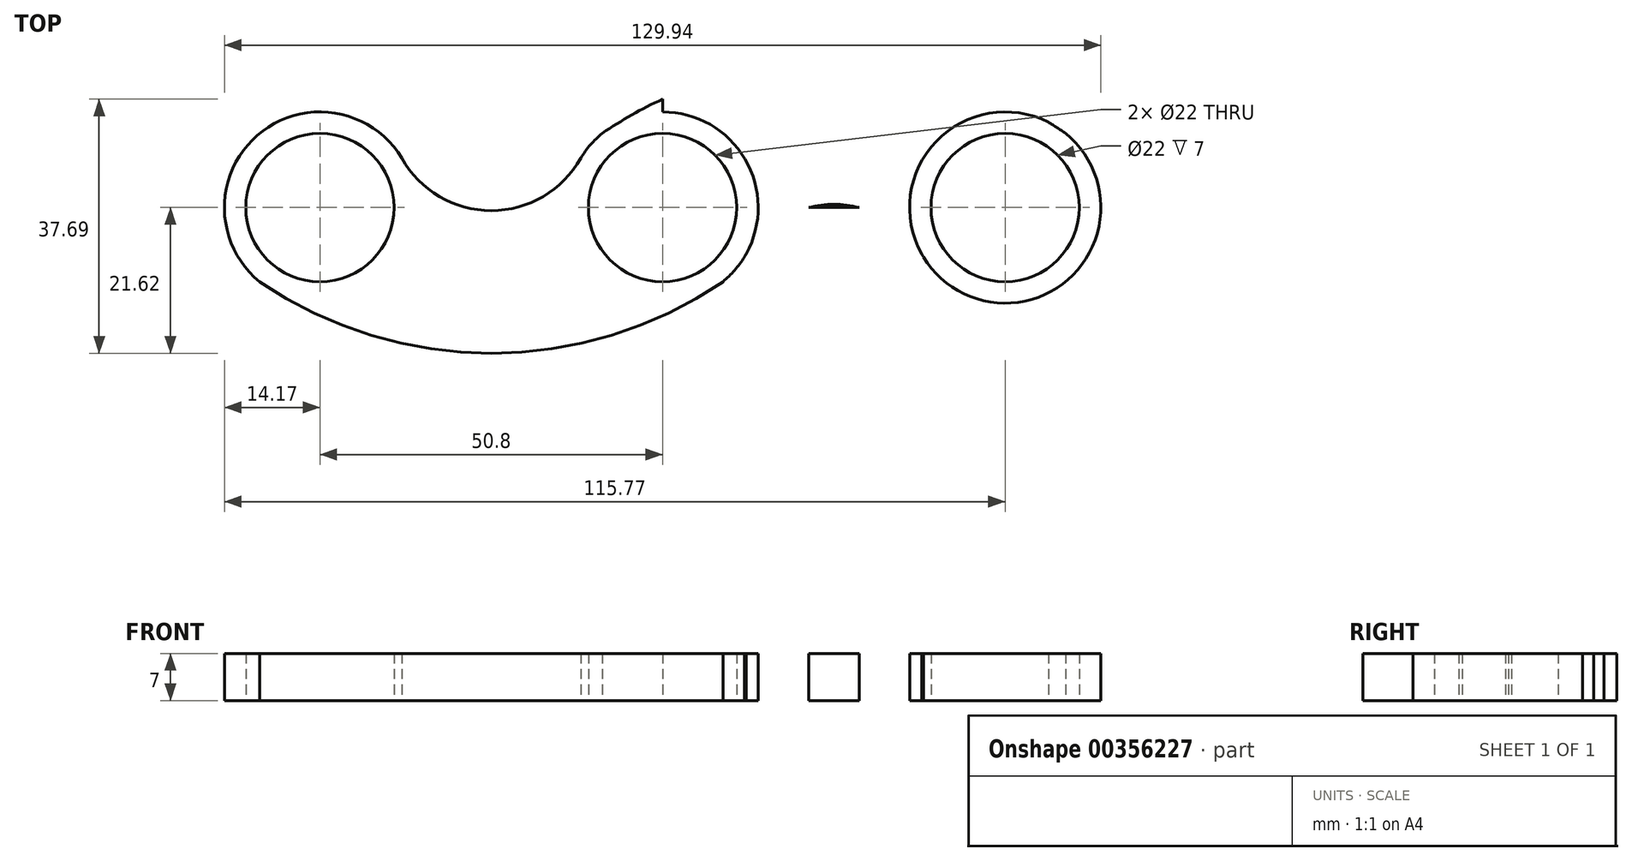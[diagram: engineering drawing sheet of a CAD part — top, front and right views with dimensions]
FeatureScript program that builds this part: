
annotation { "Feature Type Name" : "Feature", "Feature Type Description" : "" }
export const myFeature = defineFeature(function(context is Context, id is Id, definition is map)
    precondition{}
    {
        {
            var Q0;
            Q0=qCreatedBy(makeId("Top.planeOp"),FACE);
            var sketch = newSketch(context, id + "F0", { "sketchPlane" : qUnion([Q0])});
            skCircle(sketch, "E0", {"center": v(0, 0) * mm, "radius": 11 * mm});
            skLineSegment(sketch, "E1", {"start": v(0, 0) * mm, "end": v(-50.8, 0) * mm});
            skLineSegment(sketch, "E2", {"start": v(0, 0) * mm, "end": v(50.8, 0) * mm});
            skCircle(sketch, "E3", {"center": v(-50.8, 0) * mm, "radius": 11 * mm});
            skCircle(sketch, "E4", {"center": v(50.8, 0) * mm, "radius": 11 * mm});
            skCircle(sketch, "E5", {"center": v(-50.8, 0) * mm, "radius": 14.17 * mm});
            skCircle(sketch, "E6", {"center": v(50.8, 0) * mm, "radius": 14.17 * mm});
            skCircle(sketch, "E7", {"center": v(0, 0) * mm, "radius": 14.17 * mm});
            skPoint(sketch, "E8", {"position": v(0, 14.17) * mm});
            skPoint(sketch, "E9", {"position": v(-50.8, 14.17) * mm});
            skPoint(sketch, "E10", {"position": v(-41.86, 11) * mm});
            skPoint(sketch, "E11", {"position": v(-8.94, 11) * mm});
            skPoint(sketch, "E12", {"position": v(-38.67, 7.33) * mm});
            skPoint(sketch, "E13", {"position": v(-12.13, 7.33) * mm});
            skPoint(sketch, "E14", {"position": v(-29.14, 0) * mm});
            skArc(sketch, "E15", {"start": v(-38.67, 7.33) * mm, "mid": v(-25.4, -0.47) * mm, "end": v(-12.13, 7.33) * mm});
            skPoint(sketch, "E16", {"position": v(-59.74, -11) * mm});
            skPoint(sketch, "E17", {"position": v(8.94, -11) * mm});
            skPoint(sketch, "E18", {"position": v(-29.14, -21.5) * mm});
            skArc(sketch, "E19", {"start": v(-59.74, -11) * mm, "mid": v(-25.4, -21.62) * mm, "end": v(8.94, -11) * mm});
            skLineSegment(sketch, "E20", {"start": v(0, 55.32) * mm, "end": v(0, -62.03) * mm});
            skPoint(sketch, "E21", {"position": v(29.13, 0) * mm});
            skPoint(sketch, "E22", {"position": v(38.67, -7.34) * mm});
            skPoint(sketch, "E23", {"position": v(12.13, -7.34) * mm});
            skPoint(sketch, "E24", {"position": v(59.74, 11) * mm});
            skPoint(sketch, "E25", {"position": v(29.13, 21.51) * mm});
            skArc(sketch, "E26", {"start": v(59.74, 11) * mm, "mid": v(25.4, 21.63) * mm, "end": v(-8.94, 11) * mm});
            skArc(sketch, "E27", {"start": v(38.67, -7.34) * mm, "mid": v(25.4, 0.47) * mm, "end": v(12.13, -7.34) * mm});
            skSolve(sketch);
        }
        {
            var Q0;
            Q0=makeQuery(id+"F0.imprint","IMPRINT",FACE,{"disambiguationData":[TD([[makeQuery(id+"F0.imprint","IMPRINT",EDGE,{"derivedFrom":sQuery(id+"F0.wireOp",EDGE,"E4")}),-1.0]])]});
            var Q1;
            {var subQ1=sQuery(id+"F0.wireOp",EDGE,"E2");var subQ5=sQuery(id+"F0.wireOp",EDGE,"E27");var subQ6=makeQuery(id+"F0.imprint","INTERSECT",VERTEX,{"disambiguationData":[OD(0.0)],"derivedFrom":[subQ1,subQ5]});Q1=makeQuery(id+"F0.imprint","IMPRINT",FACE,{"disambiguationData":[TD([[makeQuery(id+"F0.imprint","IMPRINT",EDGE,{"disambiguationData":[TD([[subQ6,1.0]])],"derivedFrom":subQ1}),1.0]])]});}
            var Q2;
            {var subQ1=sQuery(id+"F0.wireOp",EDGE,"E1");var subQ9=sQuery(id+"F0.wireOp",EDGE,"E15");var subQ12=makeQuery(id+"F0.imprint","INTERSECT",VERTEX,{"disambiguationData":[OD(0.0)],"derivedFrom":[subQ1,subQ9]});Q2=makeQuery(id+"F0.imprint","IMPRINT",FACE,{"disambiguationData":[TD([[makeQuery(id+"F0.imprint","IMPRINT",EDGE,{"disambiguationData":[TD([[subQ12,1.0]])],"derivedFrom":subQ1}),1.0]])]});}
            var Q3;
            Q3=makeQuery(id+"F0.imprint","IMPRINT",FACE,{"disambiguationData":[TD([[makeQuery(id+"F0.imprint","IMPRINT",EDGE,{"derivedFrom":sQuery(id+"F0.wireOp",EDGE,"E3")}),-1.0]])]});
            var Q4;
            {var subQ6=sQuery(id+"F0.wireOp",EDGE,"E2");var subQ7=sQuery(id+"F0.wireOp",EDGE,"E0");var subQ8=makeQuery(id+"F0.imprint","INTERSECT",VERTEX,{"derivedFrom":[subQ7,subQ6]});Q4=makeQuery(id+"F0.imprint","IMPRINT",FACE,{"disambiguationData":[TD([[makeQuery(id+"F0.imprint","IMPRINT",EDGE,{"disambiguationData":[TD([[subQ8,1.0]])],"derivedFrom":subQ7}),-1.0]])]});}
            var Q5;
            {var subQ0=sQuery(id+"F0.wireOp",EDGE,"E1");var subQ1=sQuery(id+"F0.wireOp",EDGE,"E0");var subQ2=makeQuery(id+"F0.imprint","INTERSECT",VERTEX,{"derivedFrom":[subQ1,subQ0]});Q5=makeQuery(id+"F0.imprint","IMPRINT",FACE,{"disambiguationData":[TD([[makeQuery(id+"F0.imprint","IMPRINT",EDGE,{"disambiguationData":[TD([[subQ2,-1.0]])],"derivedFrom":subQ1}),-1.0]])]});}
            var Q6;
            {var subQ6=sQuery(id+"F0.wireOp",EDGE,"E20");var subQ9=sQuery(id+"F0.wireOp",EDGE,"E0");var subQ12=makeQuery(id+"F0.imprint","INTERSECT",VERTEX,{"disambiguationData":[OD(0.0)],"derivedFrom":[subQ9,subQ6]});Q6=makeQuery(id+"F0.imprint","IMPRINT",FACE,{"disambiguationData":[TD([[makeQuery(id+"F0.imprint","IMPRINT",EDGE,{"disambiguationData":[TD([[subQ12,-1.0]])],"derivedFrom":subQ9}),-1.0]])]});}
            var Q7;
            {var subQ0=sQuery(id+"F0.wireOp",EDGE,"E27");var subQ1=sQuery(id+"F0.wireOp",EDGE,"E2");var subQ2=makeQuery(id+"F0.imprint","INTERSECT",VERTEX,{"disambiguationData":[OD(0.0)],"derivedFrom":[subQ1,subQ0]});Q7=makeQuery(id+"F0.imprint","IMPRINT",FACE,{"disambiguationData":[TD([[makeQuery(id+"F0.imprint","IMPRINT",EDGE,{"disambiguationData":[TD([[subQ2,1.0]])],"derivedFrom":subQ1}),-1.0]])]});}
            var Q8;
            {var subQ0=sQuery(id+"F0.wireOp",EDGE,"E20");var subQ1=sQuery(id+"F0.wireOp",EDGE,"E0");var subQ2=makeQuery(id+"F0.imprint","INTERSECT",VERTEX,{"disambiguationData":[OD(0.0)],"derivedFrom":[subQ1,subQ0]});Q8=makeQuery(id+"F0.imprint","IMPRINT",FACE,{"disambiguationData":[TD([[makeQuery(id+"F0.imprint","IMPRINT",EDGE,{"disambiguationData":[TD([[subQ2,1.0]])],"derivedFrom":subQ1}),-1.0]])]});}
            var Q9;
            {var subQ0=sQuery(id+"F0.wireOp",EDGE,"E26");var subQ1=sQuery(id+"F0.wireOp",EDGE,"E7");var subQ2=makeQuery(id+"F0.imprint","INTERSECT",VERTEX,{"disambiguationData":[OD(1.0)],"derivedFrom":[subQ1,subQ0]});Q9=makeQuery(id+"F0.imprint","IMPRINT",FACE,{"disambiguationData":[TD([[makeQuery(id+"F0.imprint","IMPRINT",EDGE,{"disambiguationData":[TD([[subQ2,1.0]])],"derivedFrom":subQ1}),-1.0]])]});}
            var Q10;
            {var subQ0=sQuery(id+"F0.wireOp",EDGE,"E15");var subQ1=sQuery(id+"F0.wireOp",EDGE,"E1");var subQ2=makeQuery(id+"F0.imprint","INTERSECT",VERTEX,{"disambiguationData":[OD(0.0)],"derivedFrom":[subQ1,subQ0]});Q10=makeQuery(id+"F0.imprint","IMPRINT",FACE,{"disambiguationData":[TD([[makeQuery(id+"F0.imprint","IMPRINT",EDGE,{"disambiguationData":[TD([[subQ2,1.0]])],"derivedFrom":subQ1}),-1.0]])]});}
            var Q11;
            {var subQ0=sQuery(id+"F0.wireOp",EDGE,"E15");var subQ1=sQuery(id+"F0.wireOp",EDGE,"E1");var subQ2=makeQuery(id+"F0.imprint","INTERSECT",VERTEX,{"disambiguationData":[OD(1.0)],"derivedFrom":[subQ1,subQ0]});Q11=makeQuery(id+"F0.imprint","IMPRINT",FACE,{"disambiguationData":[TD([[makeQuery(id+"F0.imprint","IMPRINT",EDGE,{"disambiguationData":[TD([[subQ2,-1.0]])],"derivedFrom":subQ1}),-1.0]])]});}
            var Q12;
            {var subQ0=sQuery(id+"F0.wireOp",EDGE,"E19");var subQ1=sQuery(id+"F0.wireOp",EDGE,"E7");var subQ2=makeQuery(id+"F0.imprint","INTERSECT",VERTEX,{"disambiguationData":[OD(1.0)],"derivedFrom":[subQ1,subQ0]});Q12=makeQuery(id+"F0.imprint","IMPRINT",FACE,{"disambiguationData":[TD([[makeQuery(id+"F0.imprint","IMPRINT",EDGE,{"disambiguationData":[TD([[subQ2,1.0]])],"derivedFrom":subQ1}),-1.0]])]});}
            var Q13;
            {var subQ0=sQuery(id+"F0.wireOp",EDGE,"E27");var subQ1=sQuery(id+"F0.wireOp",EDGE,"E2");var subQ2=makeQuery(id+"F0.imprint","INTERSECT",VERTEX,{"disambiguationData":[OD(1.0)],"derivedFrom":[subQ1,subQ0]});Q13=makeQuery(id+"F0.imprint","IMPRINT",FACE,{"disambiguationData":[TD([[makeQuery(id+"F0.imprint","IMPRINT",EDGE,{"disambiguationData":[TD([[subQ2,-1.0]])],"derivedFrom":subQ1}),-1.0]])]});}
            extrude(context, id + "F1", {"entities" : qUnion([Q0, Q1, Q2, Q3, Q4, Q5, Q6, Q7, Q8, Q9, Q10, Q11, Q12, Q13]), "depth" : 7 * mm});
        }
    });
